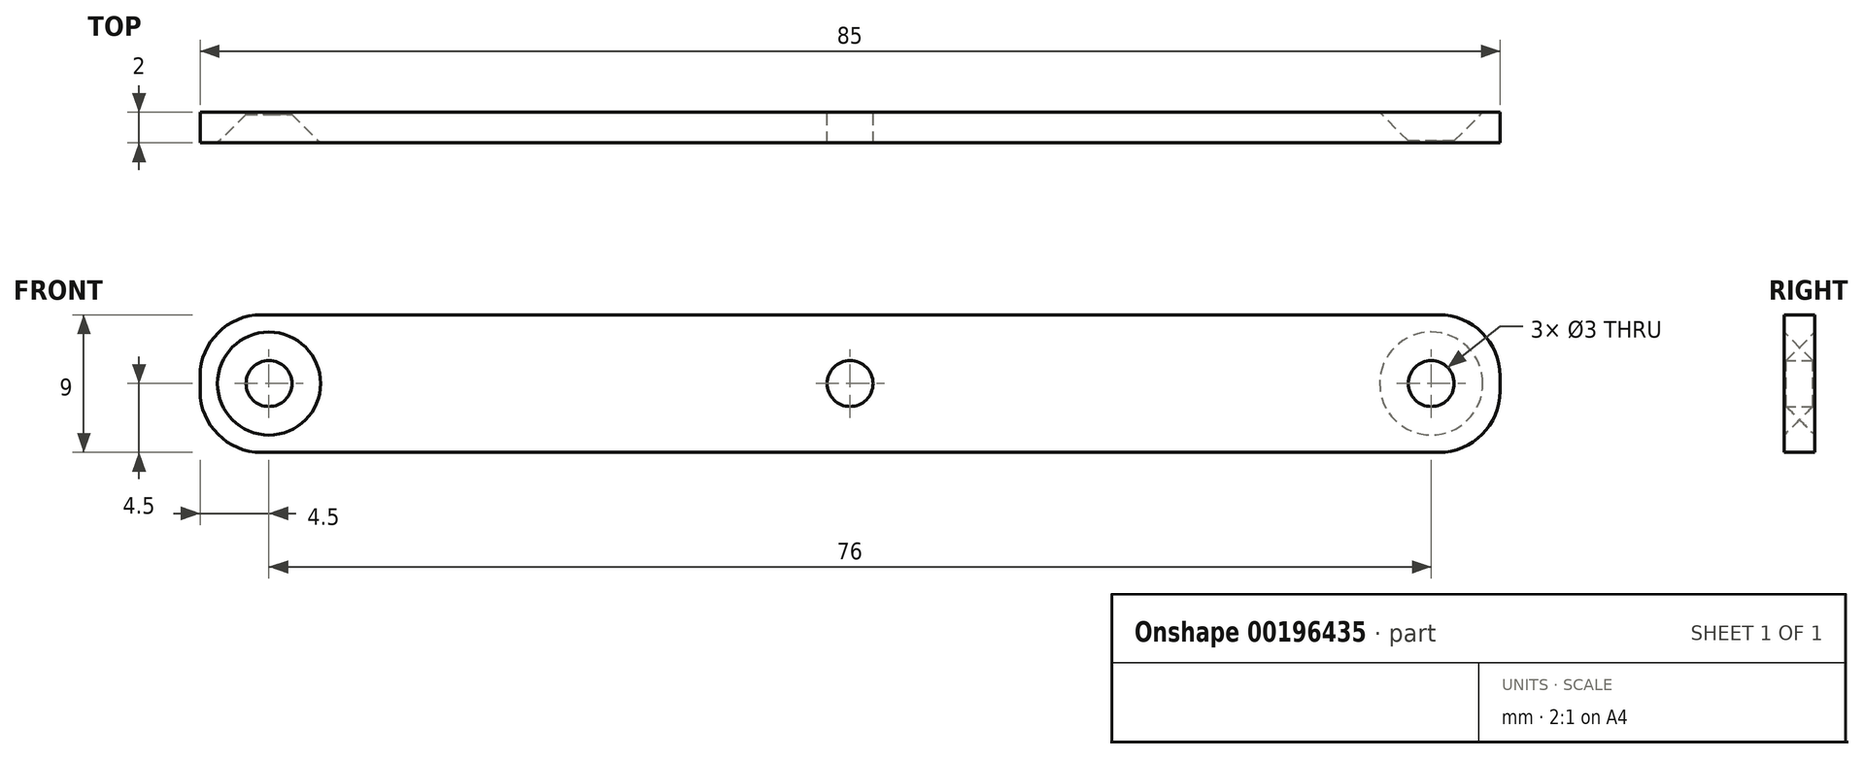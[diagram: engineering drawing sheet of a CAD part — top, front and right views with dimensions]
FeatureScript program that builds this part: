
annotation { "Feature Type Name" : "Feature", "Feature Type Description" : "" }
export const myFeature = defineFeature(function(context is Context, id is Id, definition is map)
    precondition{}
    {
        {
            var Q0;
            Q0=qCreatedBy(makeId("Front.planeOp"),FACE);
            var sketch = newSketch(context, id + "F0", { "sketchPlane" : qUnion([Q0])});
            skLineSegment(sketch, "E0.bottom", {"start": v(42.5, 4.5) * mm, "end": v(-42.5, 4.5) * mm});
            skLineSegment(sketch, "E0.top", {"start": v(42.5, -4.5) * mm, "end": v(-42.5, -4.5) * mm});
            skLineSegment(sketch, "E0.left", {"start": v(42.5, 4.5) * mm, "end": v(42.5, -4.5) * mm});
            skLineSegment(sketch, "E0.right", {"start": v(-42.5, 4.5) * mm, "end": v(-42.5, -4.5) * mm});
            skPoint(sketch, "E0.middle", {"position": v(0, 0) * mm});
            skCircle(sketch, "E1", {"center": v(0, 0) * mm, "radius": 1.5 * mm});
            skCircle(sketch, "E2", {"center": v(38, 0) * mm, "radius": 1.5 * mm});
            skCircle(sketch, "E3", {"center": v(-38, 0) * mm, "radius": 1.5 * mm});
            skSolve(sketch);
        }
        {
            var Q0;
            Q0=qSketchRegion(id+"F0",true);
            extrude(context, id + "F1", {"entities" : qUnion([Q0]), "depth" : 2 * mm});
        }
        {
            var Q0;
            Q0=makeQuery(id+"F1.opExtrude","SWEPT_EDGE",EDGE,{"disambiguationData":[OSD([sQuery(id+"F0.wireOp",EDGE,"E0.bottom"),sQuery(id+"F0.wireOp",EDGE,"E0.right")])]});
            var Q1;
            Q1=makeQuery(id+"F1.opExtrude","SWEPT_EDGE",EDGE,{"disambiguationData":[OSD([sQuery(id+"F0.wireOp",EDGE,"E0.top"),sQuery(id+"F0.wireOp",EDGE,"E0.right")])]});
            var Q2;
            Q2=makeQuery(id+"F1.opExtrude","SWEPT_EDGE",EDGE,{"disambiguationData":[OSD([sQuery(id+"F0.wireOp",EDGE,"E0.top"),sQuery(id+"F0.wireOp",EDGE,"E0.left")])]});
            var Q3;
            Q3=makeQuery(id+"F1.opExtrude","SWEPT_EDGE",EDGE,{"disambiguationData":[OSD([sQuery(id+"F0.wireOp",EDGE,"E0.bottom"),sQuery(id+"F0.wireOp",EDGE,"E0.left")])]});
            fillet(context, id + "F2", {"entities" : qUnion([Q0, Q1, Q2, Q3]), "radius" : 4 * mm, "tangentPropagation" : true, "allowEdgeOverflow" : false});
        }
        {
            var Q0;
            Q0=makeQuery(id+"F1.opExtrude","CAP_EDGE",EDGE,{"disambiguationData":[OSD([sQuery(id+"F0.wireOp",EDGE,"E3")])],"isStart":false});
            var Q1;
            Q1=makeQuery(id+"F1.opExtrude","CAP_EDGE",EDGE,{"disambiguationData":[OSD([sQuery(id+"F0.wireOp",EDGE,"E2")])],"isStart":true});
            chamfer(context, id + "F3", {"entities" : qUnion([Q0, Q1]), "width" : 1.87 * mm, "tangentPropagation" : true});
        }
    });
